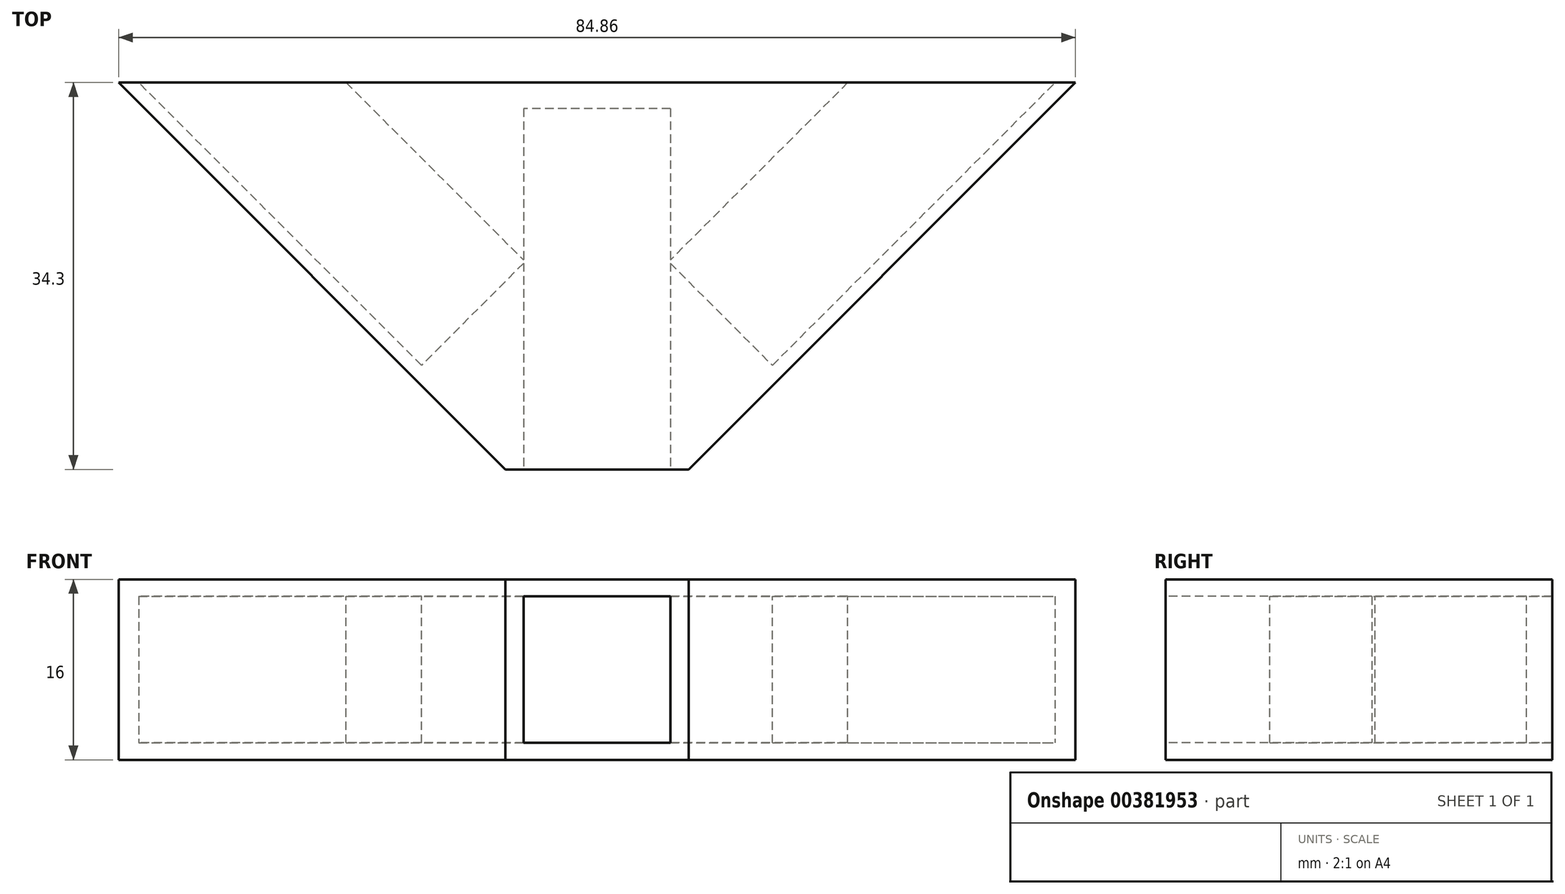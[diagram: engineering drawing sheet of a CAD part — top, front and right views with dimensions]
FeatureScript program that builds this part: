
annotation { "Feature Type Name" : "Feature", "Feature Type Description" : "" }
export const myFeature = defineFeature(function(context is Context, id is Id, definition is map)
    precondition{}
    {
        {
            var Q0;
            Q0=qCreatedBy(makeId("Top.planeOp"),FACE);
            var sketch = newSketch(context, id + "F0", { "sketchPlane" : qUnion([Q0])});
            skLineSegment(sketch, "E0", {"start": v(0, 0) * mm, "end": v(-42.43, 42.43) * mm});
            skLineSegment(sketch, "E1", {"start": v(-42.43, 42.43) * mm, "end": v(42.43, 42.43) * mm});
            skLineSegment(sketch, "E2", {"start": v(42.43, 42.43) * mm, "end": v(0, 0) * mm});
            skSolve(sketch);
        }
        {
            var Q0;
            Q0 = qSketchRegion(id + "F0", true);
            extrude(context, id + "F1", {"entities" : qUnion([Q0]), "depth" : 16 * mm});
        }
        {
            var Q0;
            Q0=makeQuery(id+"F1.opExtrude","CAP_FACE",FACE,{"disambiguationData":[OSD([sQuery(id+"F0.wireOp",EDGE,"E0"),sQuery(id+"F0.wireOp",EDGE,"E1"),sQuery(id+"F0.wireOp",EDGE,"E2")])],"isStart":false});
            var sketch = newSketch(context, id + "F2", { "sketchPlane" : qUnion([Q0])});
            skLineSegment(sketch, "E3", {"start": v(0, 1.8) * mm, "end": v(-51.27, 53.07) * mm});
            skLineSegment(sketch, "E4", {"start": v(-51.27, 53.07) * mm, "end": v(-42.08, 62.26) * mm});
            skLineSegment(sketch, "E5", {"start": v(-42.08, 62.26) * mm, "end": v(-6.36, 26.55) * mm});
            skLineSegment(sketch, "E6", {"start": v(-6.36, 26.55) * mm, "end": v(-15.56, 17.36) * mm});
            skLineSegment(sketch, "E7", {"start": v(0, 1.8) * mm, "end": v(49.04, 50.84) * mm});
            skLineSegment(sketch, "E8", {"start": v(49.04, 50.84) * mm, "end": v(39.84, 60.03) * mm});
            skLineSegment(sketch, "E9", {"start": v(39.84, 60.03) * mm, "end": v(6.36, 26.55) * mm});
            skLineSegment(sketch, "E10", {"start": v(6.36, 26.55) * mm, "end": v(15.56, 17.36) * mm});
            skSolve(sketch);
        }
        {
            var Q0;
            Q0 = qSketchRegion(id + "F2", true);
            extrude(context, id + "F3", {"entities" : qUnion([Q0]), "operationType" : NewBodyOperationType.REMOVE, "oppositeDirection" : true, "depth" : 14.5 * mm, "hasSecondDirection" : true, "secondDirectionOppositeDirection" : true, "secondDirectionDepth" : 1.5 * mm});
        }
        {
            var Q0;
            Q0=makeQuery(id+"F1.opExtrude","SWEPT_EDGE",EDGE,{"disambiguationData":[OSD([sQuery(id+"F0.wireOp",EDGE,"E0"),sQuery(id+"F0.wireOp",EDGE,"E2")])]});
            chamfer(context, id + "F4", {"entities" : qUnion([Q0]), "width" : 11.5 * mm, "tangentPropagation" : true});
        }
        {
            var Q0;
            Q0=makeQuery(id+"F4.opChamfer","BLEND_FACE",FACE,{"disambiguationData":[OSD([sQuery(id+"F0.wireOp",EDGE,"E0"),sQuery(id+"F0.wireOp",EDGE,"E2")])]});
            var sketch = newSketch(context, id + "F5", { "sketchPlane" : qUnion([Q0])});
            skLineSegment(sketch, "E11.bottom", {"start": v(6.5, 1.5) * mm, "end": v(-6.5, 1.5) * mm});
            skLineSegment(sketch, "E11.top", {"start": v(6.5, 14.5) * mm, "end": v(-6.5, 14.5) * mm});
            skLineSegment(sketch, "E11.left", {"start": v(6.5, 1.5) * mm, "end": v(6.5, 14.5) * mm});
            skLineSegment(sketch, "E11.right", {"start": v(-6.5, 1.5) * mm, "end": v(-6.5, 14.5) * mm});
            skPoint(sketch, "E11.middle", {"position": v(0, 8) * mm});
            skPoint(sketch, "E11.middle.positionSnap0", {"position": v(8.13, 8) * mm});
            skPoint(sketch, "E11.centerSnap0", {"position": v(8.13, 8) * mm});
            skSolve(sketch);
        }
        {
            var Q0;
            Q0 = qSketchRegion(id + "F5", true);
            extrude(context, id + "F6", {"entities" : qUnion([Q0]), "operationType" : NewBodyOperationType.REMOVE, "oppositeDirection" : true, "depth" : 32 * mm});
        }
    });
